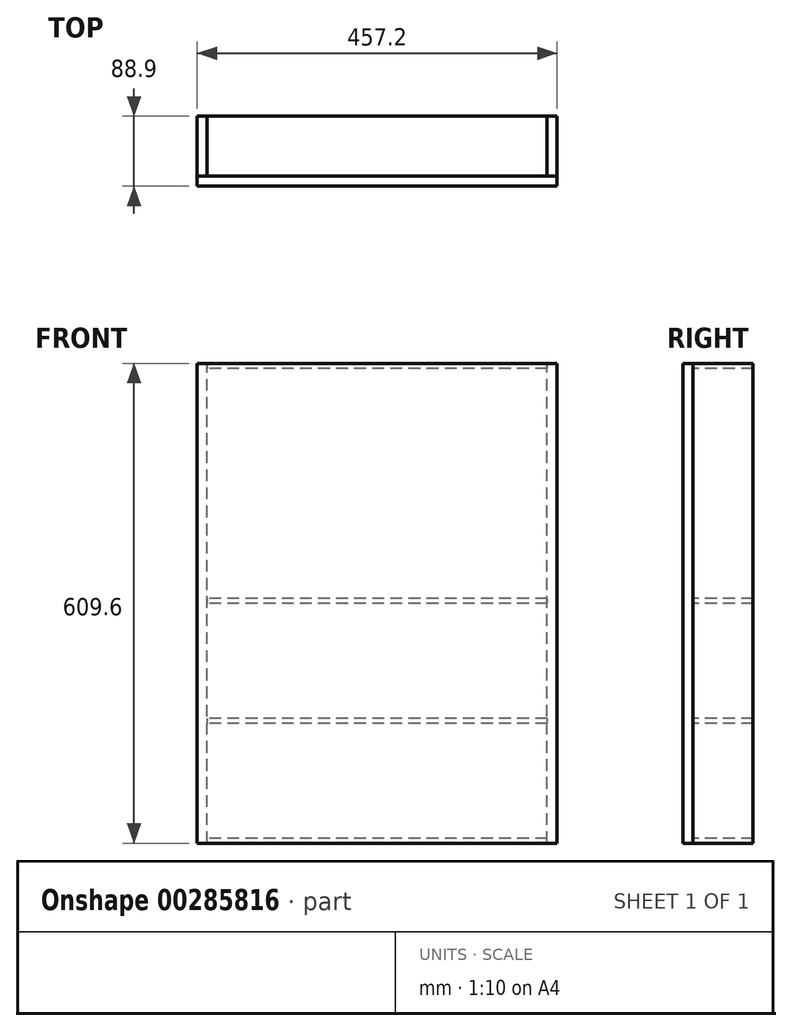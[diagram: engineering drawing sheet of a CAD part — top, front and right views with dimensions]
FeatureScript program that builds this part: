
annotation { "Feature Type Name" : "Feature", "Feature Type Description" : "" }
export const myFeature = defineFeature(function(context is Context, id is Id, definition is map)
    precondition{}
    {
        {
            var Q0;
            Q0=qCreatedBy(makeId("Front.planeOp"),FACE);
            var sketch = newSketch(context, id + "F0", { "sketchPlane" : qUnion([Q0])});
            skLineSegment(sketch, "E0.bottom", {"start": v(0, 0) * mm, "end": v(457.2, 0) * mm});
            skLineSegment(sketch, "E0.top", {"start": v(0, 609.6) * mm, "end": v(457.2, 609.6) * mm});
            skLineSegment(sketch, "E0.left", {"start": v(0, 0) * mm, "end": v(0, 609.6) * mm});
            skLineSegment(sketch, "E0.right", {"start": v(457.2, 0) * mm, "end": v(457.2, 609.6) * mm});
            skSolve(sketch);
        }
        {
            var Q0;
            Q0 = qSketchRegion(id + "F0", true);
            extrude(context, id + "F1", {"entities" : qUnion([Q0]), "depth" : 12.7 * mm});
        }
        {
            var Q0;
            Q0=makeQuery(id+"F1.opExtrude","CAP_FACE",FACE,{"disambiguationData":[OSD([sQuery(id+"F0.wireOp",EDGE,"E0.bottom"),sQuery(id+"F0.wireOp",EDGE,"E0.top"),sQuery(id+"F0.wireOp",EDGE,"E0.left"),sQuery(id+"F0.wireOp",EDGE,"E0.right")])],"isStart":true});
            var sketch = newSketch(context, id + "F2", { "sketchPlane" : qUnion([Q0])});
            skLineSegment(sketch, "E1.bottom", {"start": v(0, 0) * mm, "end": v(-12.7, 0) * mm});
            skLineSegment(sketch, "E1.top", {"start": v(0, 609.6) * mm, "end": v(-12.7, 609.6) * mm});
            skLineSegment(sketch, "E1.left", {"start": v(0, 0) * mm, "end": v(0, 609.6) * mm});
            skLineSegment(sketch, "E1.right", {"start": v(-12.7, 0) * mm, "end": v(-12.7, 609.6) * mm});
            skLineSegment(sketch, "E2.bottom", {"start": v(-457.2, 0) * mm, "end": v(-444.5, 0) * mm});
            skLineSegment(sketch, "E2.top", {"start": v(-457.2, 609.6) * mm, "end": v(-444.5, 609.6) * mm});
            skLineSegment(sketch, "E2.left", {"start": v(-457.2, 0) * mm, "end": v(-457.2, 609.6) * mm});
            skLineSegment(sketch, "E2.right", {"start": v(-444.5, 0) * mm, "end": v(-444.5, 609.6) * mm});
            skSolve(sketch);
        }
        {
            var Q0;
            Q0 = qSketchRegion(id + "F2", true);
            extrude(context, id + "F3", {"entities" : qUnion([Q0]), "depth" : 76.2 * mm});
        }
        {
            var Q0;
            Q0=makeQuery(id+"F1.opExtrude","CAP_FACE",FACE,{"disambiguationData":[OSD([sQuery(id+"F0.wireOp",EDGE,"E0.bottom"),sQuery(id+"F0.wireOp",EDGE,"E0.top"),sQuery(id+"F0.wireOp",EDGE,"E0.left"),sQuery(id+"F0.wireOp",EDGE,"E0.right")])],"isStart":true});
            var sketch = newSketch(context, id + "F4", { "sketchPlane" : qUnion([Q0])});
            skLineSegment(sketch, "E3.bottom", {"start": v(-444.5, 0) * mm, "end": v(-12.7, 0) * mm});
            skLineSegment(sketch, "E3.top", {"start": v(-444.5, 6.35) * mm, "end": v(-12.7, 6.35) * mm});
            skLineSegment(sketch, "E3.left", {"start": v(-444.5, 0) * mm, "end": v(-444.5, 6.35) * mm});
            skLineSegment(sketch, "E3.right", {"start": v(-12.7, 0) * mm, "end": v(-12.7, 6.35) * mm});
            skLineSegment(sketch, "E4.bottom", {"start": v(-444.5, 609.6) * mm, "end": v(-12.7, 609.6) * mm});
            skLineSegment(sketch, "E4.top", {"start": v(-444.5, 603.25) * mm, "end": v(-12.7, 603.25) * mm});
            skLineSegment(sketch, "E4.left", {"start": v(-444.5, 609.6) * mm, "end": v(-444.5, 603.25) * mm});
            skLineSegment(sketch, "E4.right", {"start": v(-12.7, 609.6) * mm, "end": v(-12.7, 603.25) * mm});
            skLineSegment(sketch, "E5.bottom", {"start": v(-444.5, 158.75) * mm, "end": v(-12.7, 158.75) * mm});
            skLineSegment(sketch, "E5.top", {"start": v(-444.5, 152.4) * mm, "end": v(-12.7, 152.4) * mm});
            skLineSegment(sketch, "E5.left", {"start": v(-444.5, 158.75) * mm, "end": v(-444.5, 152.4) * mm});
            skLineSegment(sketch, "E5.right", {"start": v(-12.7, 158.75) * mm, "end": v(-12.7, 152.4) * mm});
            skLineSegment(sketch, "E6.bottom", {"start": v(-444.5, 311.15) * mm, "end": v(-12.7, 311.15) * mm});
            skLineSegment(sketch, "E6.top", {"start": v(-444.5, 304.8) * mm, "end": v(-12.7, 304.8) * mm});
            skLineSegment(sketch, "E6.left", {"start": v(-444.5, 311.15) * mm, "end": v(-444.5, 304.8) * mm});
            skLineSegment(sketch, "E6.right", {"start": v(-12.7, 311.15) * mm, "end": v(-12.7, 304.8) * mm});
            skSolve(sketch);
        }
        {
            var Q0;
            Q0 = qSketchRegion(id + "F4", true);
            extrude(context, id + "F5", {"entities" : qUnion([Q0]), "depth" : 76.2 * mm});
        }
    });
